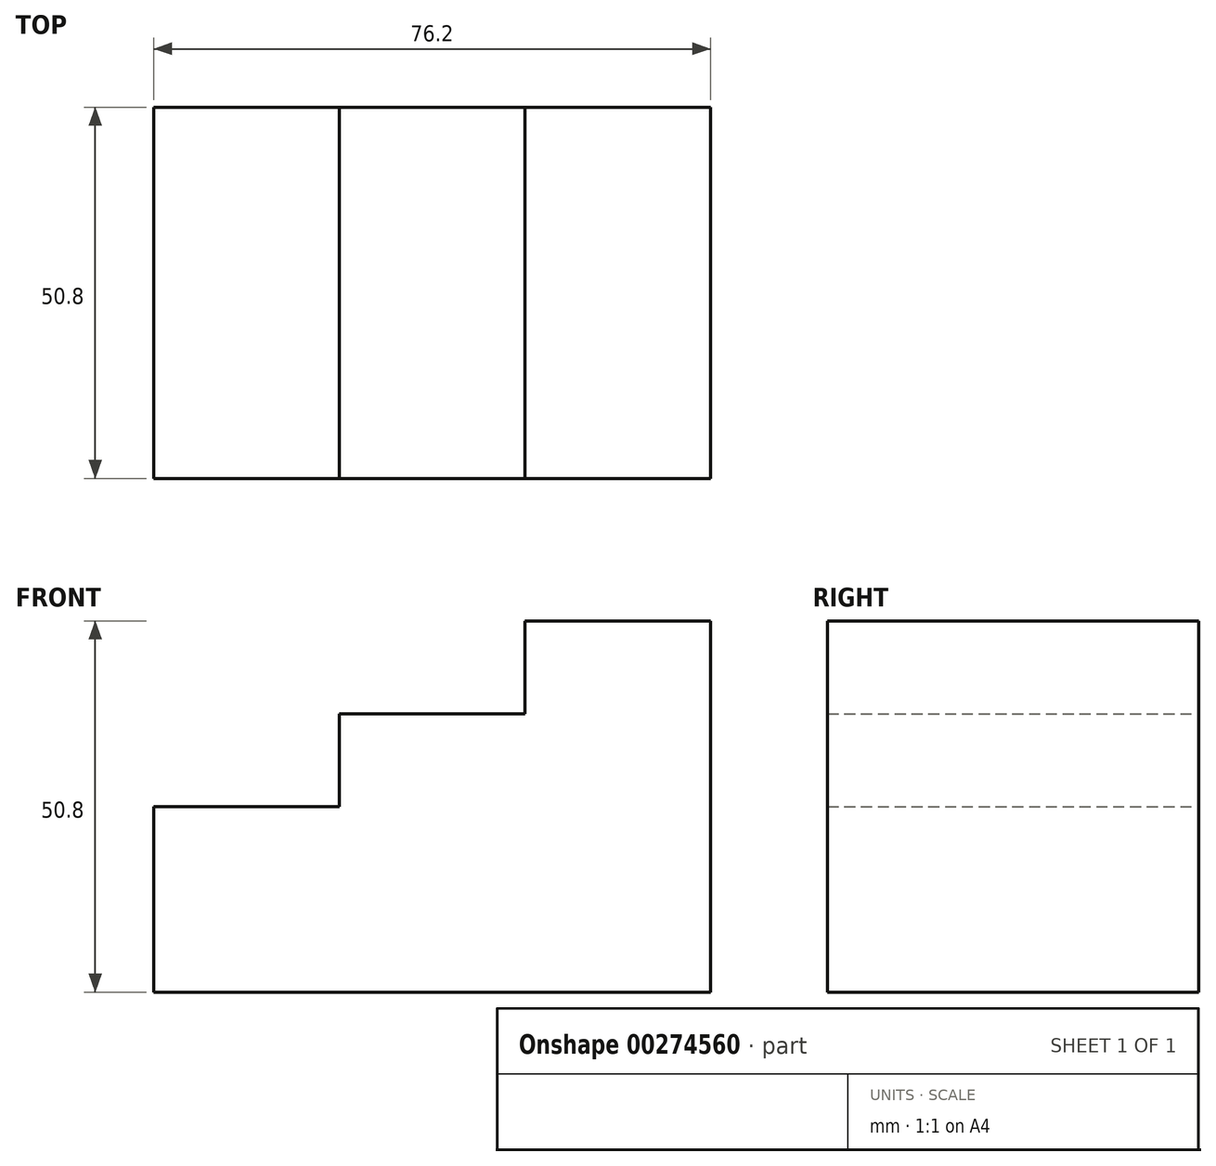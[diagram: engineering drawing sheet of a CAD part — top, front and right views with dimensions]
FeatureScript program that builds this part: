
annotation { "Feature Type Name" : "Feature", "Feature Type Description" : "" }
export const myFeature = defineFeature(function(context is Context, id is Id, definition is map)
    precondition{}
    {
        {
            var Q0;
            Q0=qCreatedBy(makeId("Front.planeOp"),FACE);
            var sketch = newSketch(context, id + "F0", { "sketchPlane" : qUnion([Q0])});
            skLineSegment(sketch, "E0", {"start": v(0, 0) * mm, "end": v(-76.2, 0) * mm});
            skLineSegment(sketch, "E1", {"start": v(-76.2, 0) * mm, "end": v(-76.2, 25.4) * mm});
            skLineSegment(sketch, "E2", {"start": v(-76.2, 25.4) * mm, "end": v(-50.8, 25.4) * mm});
            skLineSegment(sketch, "E3", {"start": v(-50.8, 25.4) * mm, "end": v(-50.8, 38.1) * mm});
            skLineSegment(sketch, "E4", {"start": v(-50.8, 38.1) * mm, "end": v(-25.4, 38.1) * mm});
            skLineSegment(sketch, "E5", {"start": v(-25.4, 38.1) * mm, "end": v(-25.4, 50.8) * mm});
            skLineSegment(sketch, "E6", {"start": v(-25.4, 50.8) * mm, "end": v(0, 50.8) * mm});
            skLineSegment(sketch, "E7", {"start": v(0, 50.8) * mm, "end": v(0, 0) * mm});
            skSolve(sketch);
        }
        {
            var Q0;
            Q0 = qSketchRegion(id + "F0", true);
            extrude(context, id + "F1", {"entities" : qUnion([Q0]), "depth" : 50.8 * mm});
        }
    });
